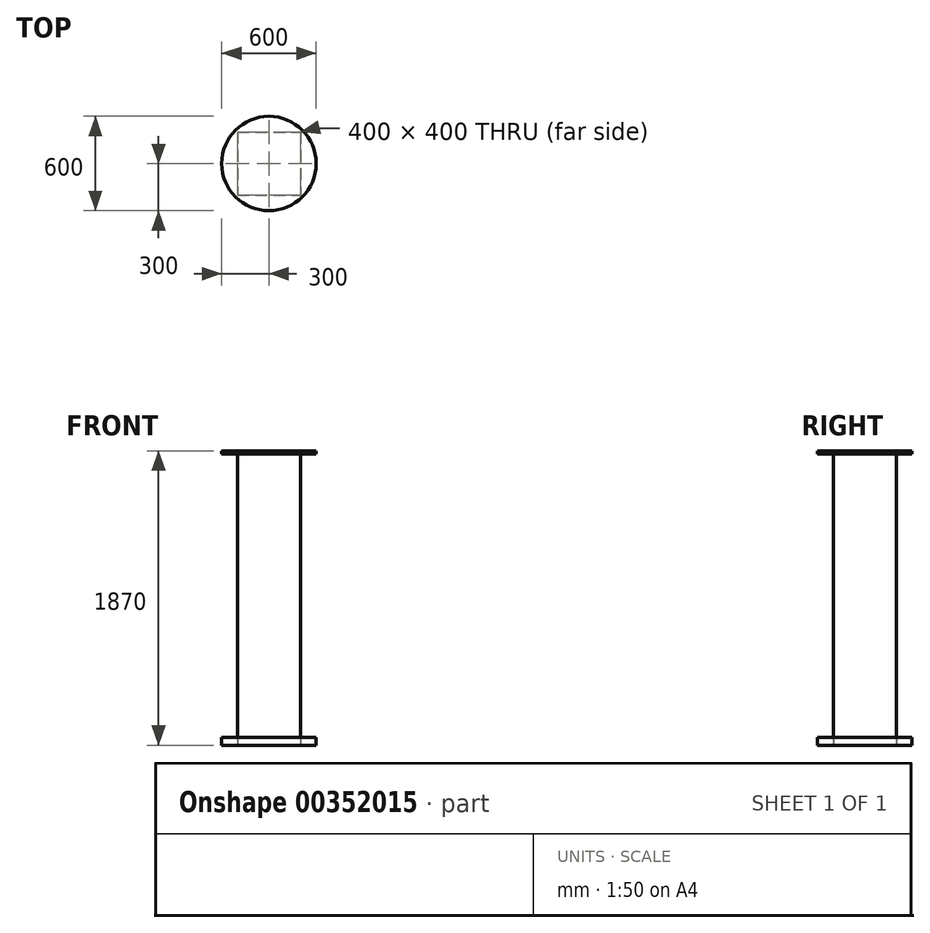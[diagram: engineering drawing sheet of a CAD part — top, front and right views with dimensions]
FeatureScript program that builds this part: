
annotation { "Feature Type Name" : "Feature", "Feature Type Description" : "" }
export const myFeature = defineFeature(function(context is Context, id is Id, definition is map)
    precondition{}
    {
        {
            var Q0;
            Q0=qCreatedBy(makeId("Top.planeOp"),FACE);
            var sketch = newSketch(context, id + "F0", { "sketchPlane" : qUnion([Q0])});
            skCircle(sketch, "E0", {"center": v(0, 0) * mm, "radius": 300 * mm});
            skLineSegment(sketch, "E1.bottom", {"start": v(-200, 200) * mm, "end": v(200, 200) * mm});
            skLineSegment(sketch, "E1.top", {"start": v(-200, -200) * mm, "end": v(200, -200) * mm});
            skLineSegment(sketch, "E1.left", {"start": v(-200, 200) * mm, "end": v(-200, -200) * mm});
            skLineSegment(sketch, "E1.right", {"start": v(200, 200) * mm, "end": v(200, -200) * mm});
            skSolve(sketch);
        }
        {
            var Q0;
            Q0=makeQuery(id+"F0.imprint","IMPRINT",FACE,{"disambiguationData":[TD([[makeQuery(id+"F0.imprint","IMPRINT",EDGE,{"derivedFrom":sQuery(id+"F0.wireOp",EDGE,"E0")}),1.0]])]});
            var Q1;
            Q1=makeQuery(id+"F0.imprint","IMPRINT",FACE,{"disambiguationData":[TD([[makeQuery(id+"F0.imprint","IMPRINT",EDGE,{"derivedFrom":sQuery(id+"F0.wireOp",EDGE,"E1.bottom")}),-1.0]])]});
            var Q2;
            Q2=sQuery(id+"F0.wireOp",EDGE,"E0");
            extrude(context, id + "F1", {"entities" : qUnion([Q0, Q1]), "surfaceEntities" : qUnion([Q2]), "depth" : 1870 * mm, "hasSecondDirection" : true, "secondDirectionOppositeDirection" : true, "secondDirectionDepth" : -1850 * mm});
        }
        {
            var Q0;
            Q0=makeQuery(id+"F0.imprint","IMPRINT",FACE,{"disambiguationData":[TD([[makeQuery(id+"F0.imprint","IMPRINT",EDGE,{"derivedFrom":sQuery(id+"F0.wireOp",EDGE,"E1.bottom")}),-1.0]])]});
            extrude(context, id + "F2", {"entities" : qUnion([Q0]), "depth" : 1850 * mm});
        }
        {
            var Q0;
            Q0=makeQuery(id+"F0.imprint","IMPRINT",FACE,{"disambiguationData":[TD([[makeQuery(id+"F0.imprint","IMPRINT",EDGE,{"derivedFrom":sQuery(id+"F0.wireOp",EDGE,"E0")}),1.0]])]});
            extrude(context, id + "F3", {"entities" : qUnion([Q0]), "depth" : 50 * mm});
        }
    });
